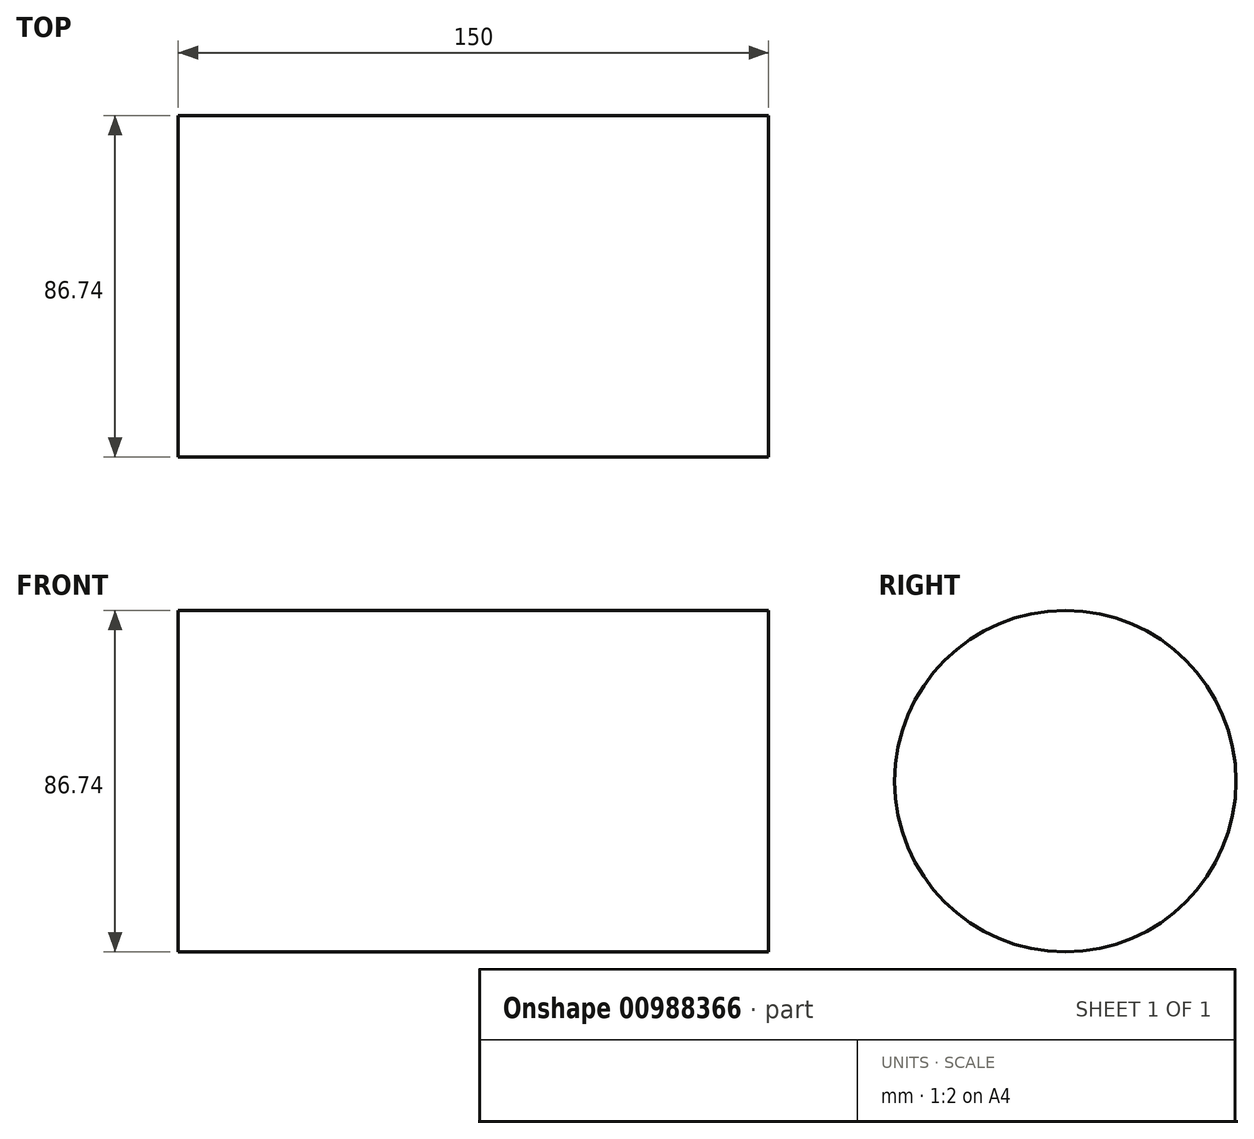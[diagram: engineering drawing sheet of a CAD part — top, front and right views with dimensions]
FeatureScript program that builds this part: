
annotation { "Feature Type Name" : "Feature", "Feature Type Description" : "" }
export const myFeature = defineFeature(function(context is Context, id is Id, definition is map)
    precondition{}
    {
        {
            var Q0;
            Q0=qCreatedBy(makeId("Right.planeOp"),FACE);
            var sketch = newSketch(context, id + "F0", { "sketchPlane" : qUnion([Q0])});
            skCircle(sketch, "E0", {"center": v(0, 0) * mm, "radius": 43.37 * mm});
            skSolve(sketch);
        }
        {
            var Q0;
            Q0=makeQuery(id+"F0.imprint","IMPRINT",FACE,{"disambiguationData":[TD([[makeQuery(id+"F0.imprint","IMPRINT",EDGE,{"derivedFrom":sQuery(id+"F0.wireOp",EDGE,"E0")}),1.0]])]});
            extrude(context, id + "F1", {"entities" : qUnion([Q0]), "depth" : 150 * mm, "offsetDistance" : 25 * mm});
        }
    });
